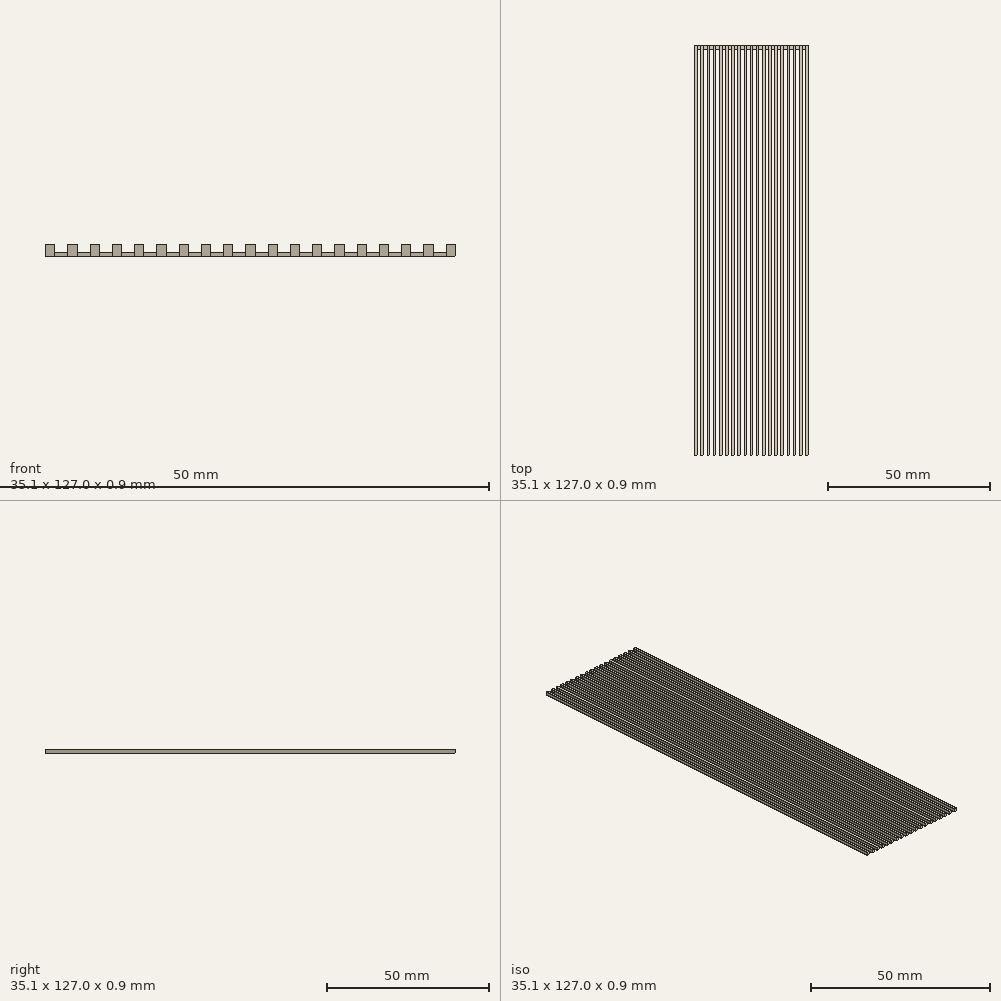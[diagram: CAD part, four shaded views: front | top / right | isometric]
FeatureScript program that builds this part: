
annotation { "Feature Type Name" : "Feature", "Feature Type Description" : "" }
export const myFeature = defineFeature(function(context is Context, id is Id, definition is map)
    precondition{}
    {
        {
            var Q0;
            Q0=qCreatedBy(makeId("Front.planeOp"),FACE);
            var sketch = newSketch(context, id + "F0", { "sketchPlane" : qUnion([Q0])});
            skLineSegment(sketch, "E0.bottom", {"start": v(0.4, -0.47) * mm, "end": v(-0.4, -0.47) * mm});
            skLineSegment(sketch, "E0.top", {"start": v(0.4, 0.47) * mm, "end": v(-0.4, 0.47) * mm});
            skLineSegment(sketch, "E0.left", {"start": v(0.4, -0.47) * mm, "end": v(0.4, 0.47) * mm});
            skLineSegment(sketch, "E0.right", {"start": v(-0.4, -0.47) * mm, "end": v(-0.4, 0.47) * mm});
            skPoint(sketch, "E0.middle", {"position": v(0, 0) * mm});
            skLineSegment(sketch, "E1.1.0.0", {"start": v(2.3, -0.47) * mm, "end": v(2.3, 0.47) * mm});
            skLineSegment(sketch, "E1.1.0.1", {"start": v(2.3, 0.47) * mm, "end": v(1.5, 0.47) * mm});
            skLineSegment(sketch, "E1.1.0.2", {"start": v(1.5, -0.47) * mm, "end": v(1.5, 0.47) * mm});
            skLineSegment(sketch, "E1.1.0.3", {"start": v(2.3, -0.47) * mm, "end": v(1.5, -0.47) * mm});
            skLineSegment(sketch, "E1.2.0.0", {"start": v(4.21, -0.47) * mm, "end": v(4.21, 0.47) * mm});
            skLineSegment(sketch, "E1.2.0.1", {"start": v(4.21, 0.47) * mm, "end": v(3.4, 0.47) * mm});
            skLineSegment(sketch, "E1.2.0.2", {"start": v(3.4, -0.47) * mm, "end": v(3.4, 0.47) * mm});
            skLineSegment(sketch, "E1.2.0.3", {"start": v(4.21, -0.47) * mm, "end": v(3.4, -0.47) * mm});
            skLineSegment(sketch, "E1.3.0.0", {"start": v(6.12, -0.47) * mm, "end": v(6.12, 0.47) * mm});
            skLineSegment(sketch, "E1.3.0.1", {"start": v(6.12, 0.47) * mm, "end": v(5.31, 0.47) * mm});
            skLineSegment(sketch, "E1.3.0.2", {"start": v(5.31, -0.47) * mm, "end": v(5.31, 0.47) * mm});
            skLineSegment(sketch, "E1.3.0.3", {"start": v(6.12, -0.47) * mm, "end": v(5.31, -0.47) * mm});
            skLineSegment(sketch, "E1.4.0.0", {"start": v(8.02, -0.47) * mm, "end": v(8.02, 0.47) * mm});
            skLineSegment(sketch, "E1.4.0.1", {"start": v(8.02, 0.47) * mm, "end": v(7.22, 0.47) * mm});
            skLineSegment(sketch, "E1.4.0.2", {"start": v(7.22, -0.47) * mm, "end": v(7.22, 0.47) * mm});
            skLineSegment(sketch, "E1.4.0.3", {"start": v(8.02, -0.47) * mm, "end": v(7.22, -0.47) * mm});
            skLineSegment(sketch, "E1.5.0.0", {"start": v(9.93, -0.47) * mm, "end": v(9.93, 0.47) * mm});
            skLineSegment(sketch, "E1.5.0.1", {"start": v(9.93, 0.47) * mm, "end": v(9.12, 0.47) * mm});
            skLineSegment(sketch, "E1.5.0.2", {"start": v(9.12, -0.47) * mm, "end": v(9.12, 0.47) * mm});
            skLineSegment(sketch, "E1.5.0.3", {"start": v(9.93, -0.47) * mm, "end": v(9.12, -0.47) * mm});
            skLineSegment(sketch, "E1.6.0.0", {"start": v(11.83, -0.47) * mm, "end": v(11.83, 0.47) * mm});
            skLineSegment(sketch, "E1.6.0.1", {"start": v(11.83, 0.47) * mm, "end": v(11.03, 0.47) * mm});
            skLineSegment(sketch, "E1.6.0.2", {"start": v(11.03, -0.47) * mm, "end": v(11.03, 0.47) * mm});
            skLineSegment(sketch, "E1.6.0.3", {"start": v(11.83, -0.47) * mm, "end": v(11.03, -0.47) * mm});
            skLineSegment(sketch, "E1.7.0.0", {"start": v(13.74, -0.47) * mm, "end": v(13.74, 0.47) * mm});
            skLineSegment(sketch, "E1.7.0.1", {"start": v(13.74, 0.47) * mm, "end": v(12.93, 0.47) * mm});
            skLineSegment(sketch, "E1.7.0.2", {"start": v(12.93, -0.47) * mm, "end": v(12.93, 0.47) * mm});
            skLineSegment(sketch, "E1.7.0.3", {"start": v(13.74, -0.47) * mm, "end": v(12.93, -0.47) * mm});
            skLineSegment(sketch, "E1.8.0.0", {"start": v(15.64, -0.47) * mm, "end": v(15.64, 0.47) * mm});
            skLineSegment(sketch, "E1.8.0.1", {"start": v(15.64, 0.47) * mm, "end": v(14.84, 0.47) * mm});
            skLineSegment(sketch, "E1.8.0.2", {"start": v(14.84, -0.47) * mm, "end": v(14.84, 0.47) * mm});
            skLineSegment(sketch, "E1.8.0.3", {"start": v(15.64, -0.47) * mm, "end": v(14.84, -0.47) * mm});
            skLineSegment(sketch, "E1.9.0.0", {"start": v(17.55, -0.47) * mm, "end": v(17.55, 0.47) * mm});
            skLineSegment(sketch, "E1.9.0.1", {"start": v(17.55, 0.47) * mm, "end": v(16.74, 0.47) * mm});
            skLineSegment(sketch, "E1.9.0.2", {"start": v(16.74, -0.47) * mm, "end": v(16.74, 0.47) * mm});
            skLineSegment(sketch, "E1.9.0.3", {"start": v(17.55, -0.47) * mm, "end": v(16.74, -0.47) * mm});
            skLineSegment(sketch, "E1.10.0.0", {"start": v(19.45, -0.47) * mm, "end": v(19.45, 0.47) * mm});
            skLineSegment(sketch, "E1.10.0.1", {"start": v(19.45, 0.47) * mm, "end": v(18.65, 0.47) * mm});
            skLineSegment(sketch, "E1.10.0.2", {"start": v(18.65, -0.47) * mm, "end": v(18.65, 0.47) * mm});
            skLineSegment(sketch, "E1.10.0.3", {"start": v(19.45, -0.47) * mm, "end": v(18.65, -0.47) * mm});
            skLineSegment(sketch, "E1.11.0.0", {"start": v(21.36, -0.47) * mm, "end": v(21.36, 0.47) * mm});
            skLineSegment(sketch, "E1.11.0.1", {"start": v(21.36, 0.47) * mm, "end": v(20.55, 0.47) * mm});
            skLineSegment(sketch, "E1.11.0.2", {"start": v(20.55, -0.47) * mm, "end": v(20.55, 0.47) * mm});
            skLineSegment(sketch, "E1.11.0.3", {"start": v(21.36, -0.47) * mm, "end": v(20.55, -0.47) * mm});
            skLineSegment(sketch, "E1.12.0.0", {"start": v(23.26, -0.47) * mm, "end": v(23.26, 0.47) * mm});
            skLineSegment(sketch, "E1.12.0.1", {"start": v(23.26, 0.47) * mm, "end": v(22.46, 0.47) * mm});
            skLineSegment(sketch, "E1.12.0.2", {"start": v(22.46, -0.47) * mm, "end": v(22.46, 0.47) * mm});
            skLineSegment(sketch, "E1.12.0.3", {"start": v(23.26, -0.47) * mm, "end": v(22.46, -0.47) * mm});
            skLineSegment(sketch, "E1.13.0.0", {"start": v(25.17, -0.47) * mm, "end": v(25.17, 0.47) * mm});
            skLineSegment(sketch, "E1.13.0.1", {"start": v(25.17, 0.47) * mm, "end": v(24.36, 0.47) * mm});
            skLineSegment(sketch, "E1.13.0.2", {"start": v(24.36, -0.47) * mm, "end": v(24.36, 0.47) * mm});
            skLineSegment(sketch, "E1.13.0.3", {"start": v(25.17, -0.47) * mm, "end": v(24.36, -0.47) * mm});
            skLineSegment(sketch, "E1.14.0.0", {"start": v(27.07, -0.47) * mm, "end": v(27.07, 0.47) * mm});
            skLineSegment(sketch, "E1.14.0.1", {"start": v(27.07, 0.47) * mm, "end": v(26.27, 0.47) * mm});
            skLineSegment(sketch, "E1.14.0.2", {"start": v(26.27, -0.47) * mm, "end": v(26.27, 0.47) * mm});
            skLineSegment(sketch, "E1.14.0.3", {"start": v(27.07, -0.47) * mm, "end": v(26.27, -0.47) * mm});
            skLineSegment(sketch, "E1.15.0.0", {"start": v(28.98, -0.47) * mm, "end": v(28.98, 0.47) * mm});
            skLineSegment(sketch, "E1.15.0.1", {"start": v(28.98, 0.47) * mm, "end": v(28.17, 0.47) * mm});
            skLineSegment(sketch, "E1.15.0.2", {"start": v(28.17, -0.47) * mm, "end": v(28.17, 0.47) * mm});
            skLineSegment(sketch, "E1.15.0.3", {"start": v(28.98, -0.47) * mm, "end": v(28.17, -0.47) * mm});
            skLineSegment(sketch, "E1.16.0.0", {"start": v(30.88, -0.47) * mm, "end": v(30.88, 0.47) * mm});
            skLineSegment(sketch, "E1.16.0.1", {"start": v(30.88, 0.47) * mm, "end": v(30.08, 0.47) * mm});
            skLineSegment(sketch, "E1.16.0.2", {"start": v(30.08, -0.47) * mm, "end": v(30.08, 0.47) * mm});
            skLineSegment(sketch, "E1.16.0.3", {"start": v(30.88, -0.47) * mm, "end": v(30.08, -0.47) * mm});
            skLineSegment(sketch, "E1.17.0.0", {"start": v(32.79, -0.47) * mm, "end": v(32.79, 0.47) * mm});
            skLineSegment(sketch, "E1.17.0.1", {"start": v(32.79, 0.47) * mm, "end": v(31.98, 0.47) * mm});
            skLineSegment(sketch, "E1.17.0.2", {"start": v(31.98, -0.47) * mm, "end": v(31.98, 0.47) * mm});
            skLineSegment(sketch, "E1.17.0.3", {"start": v(32.79, -0.47) * mm, "end": v(31.98, -0.47) * mm});
            skLineSegment(sketch, "E1.18.0.0", {"start": v(34.7, -0.47) * mm, "end": v(34.7, 0.47) * mm});
            skLineSegment(sketch, "E1.18.0.1", {"start": v(34.7, 0.47) * mm, "end": v(33.89, 0.47) * mm});
            skLineSegment(sketch, "E1.18.0.2", {"start": v(33.89, -0.47) * mm, "end": v(33.89, 0.47) * mm});
            skLineSegment(sketch, "E1.18.0.3", {"start": v(34.7, -0.47) * mm, "end": v(33.89, -0.47) * mm});
            skLineSegment(sketch, "E1.direction1", {"start": v(0.4, -0.47) * mm, "end": v(2.3, -0.47) * mm, "construction": true});
            skSolve(sketch);
        }
        {
            var Q0;
            Q0=makeQuery(id+"F0.imprint","IMPRINT",FACE,{"disambiguationData":[TD([[makeQuery(id+"F0.imprint","IMPRINT",EDGE,{"derivedFrom":sQuery(id+"F0.wireOp",EDGE,"E0.bottom")}),-1.0]])]});
            var Q1;
            Q1=makeQuery(id+"F0.imprint","IMPRINT",FACE,{"disambiguationData":[TD([[makeQuery(id+"F0.imprint","IMPRINT",EDGE,{"derivedFrom":sQuery(id+"F0.wireOp",EDGE,"E1.1.0.0")}),1.0]])]});
            var Q2;
            Q2=makeQuery(id+"F0.imprint","IMPRINT",FACE,{"disambiguationData":[TD([[makeQuery(id+"F0.imprint","IMPRINT",EDGE,{"derivedFrom":sQuery(id+"F0.wireOp",EDGE,"E1.2.0.0")}),1.0]])]});
            var Q3;
            Q3=makeQuery(id+"F0.imprint","IMPRINT",FACE,{"disambiguationData":[TD([[makeQuery(id+"F0.imprint","IMPRINT",EDGE,{"derivedFrom":sQuery(id+"F0.wireOp",EDGE,"E1.3.0.0")}),1.0]])]});
            var Q4;
            Q4=makeQuery(id+"F0.imprint","IMPRINT",FACE,{"disambiguationData":[TD([[makeQuery(id+"F0.imprint","IMPRINT",EDGE,{"derivedFrom":sQuery(id+"F0.wireOp",EDGE,"E1.4.0.0")}),1.0]])]});
            var Q5;
            Q5=makeQuery(id+"F0.imprint","IMPRINT",FACE,{"disambiguationData":[TD([[makeQuery(id+"F0.imprint","IMPRINT",EDGE,{"derivedFrom":sQuery(id+"F0.wireOp",EDGE,"E1.5.0.0")}),1.0]])]});
            var Q6;
            Q6=makeQuery(id+"F0.imprint","IMPRINT",FACE,{"disambiguationData":[TD([[makeQuery(id+"F0.imprint","IMPRINT",EDGE,{"derivedFrom":sQuery(id+"F0.wireOp",EDGE,"E1.6.0.0")}),1.0]])]});
            var Q7;
            Q7=makeQuery(id+"F0.imprint","IMPRINT",FACE,{"disambiguationData":[TD([[makeQuery(id+"F0.imprint","IMPRINT",EDGE,{"derivedFrom":sQuery(id+"F0.wireOp",EDGE,"E1.7.0.0")}),1.0]])]});
            var Q8;
            Q8=makeQuery(id+"F0.imprint","IMPRINT",FACE,{"disambiguationData":[TD([[makeQuery(id+"F0.imprint","IMPRINT",EDGE,{"derivedFrom":sQuery(id+"F0.wireOp",EDGE,"E1.8.0.0")}),1.0]])]});
            var Q9;
            Q9=makeQuery(id+"F0.imprint","IMPRINT",FACE,{"disambiguationData":[TD([[makeQuery(id+"F0.imprint","IMPRINT",EDGE,{"derivedFrom":sQuery(id+"F0.wireOp",EDGE,"E1.9.0.0")}),1.0]])]});
            var Q10;
            Q10=makeQuery(id+"F0.imprint","IMPRINT",FACE,{"disambiguationData":[TD([[makeQuery(id+"F0.imprint","IMPRINT",EDGE,{"derivedFrom":sQuery(id+"F0.wireOp",EDGE,"E1.10.0.0")}),1.0]])]});
            var Q11;
            Q11=makeQuery(id+"F0.imprint","IMPRINT",FACE,{"disambiguationData":[TD([[makeQuery(id+"F0.imprint","IMPRINT",EDGE,{"derivedFrom":sQuery(id+"F0.wireOp",EDGE,"E1.11.0.0")}),1.0]])]});
            var Q12;
            Q12=makeQuery(id+"F0.imprint","IMPRINT",FACE,{"disambiguationData":[TD([[makeQuery(id+"F0.imprint","IMPRINT",EDGE,{"derivedFrom":sQuery(id+"F0.wireOp",EDGE,"E1.12.0.0")}),1.0]])]});
            var Q13;
            Q13=makeQuery(id+"F0.imprint","IMPRINT",FACE,{"disambiguationData":[TD([[makeQuery(id+"F0.imprint","IMPRINT",EDGE,{"derivedFrom":sQuery(id+"F0.wireOp",EDGE,"E1.13.0.0")}),1.0]])]});
            var Q14;
            Q14=makeQuery(id+"F0.imprint","IMPRINT",FACE,{"disambiguationData":[TD([[makeQuery(id+"F0.imprint","IMPRINT",EDGE,{"derivedFrom":sQuery(id+"F0.wireOp",EDGE,"E1.14.0.0")}),1.0]])]});
            var Q15;
            Q15=makeQuery(id+"F0.imprint","IMPRINT",FACE,{"disambiguationData":[TD([[makeQuery(id+"F0.imprint","IMPRINT",EDGE,{"derivedFrom":sQuery(id+"F0.wireOp",EDGE,"E1.15.0.0")}),1.0]])]});
            var Q16;
            Q16=makeQuery(id+"F0.imprint","IMPRINT",FACE,{"disambiguationData":[TD([[makeQuery(id+"F0.imprint","IMPRINT",EDGE,{"derivedFrom":sQuery(id+"F0.wireOp",EDGE,"E1.16.0.0")}),1.0]])]});
            var Q17;
            Q17=makeQuery(id+"F0.imprint","IMPRINT",FACE,{"disambiguationData":[TD([[makeQuery(id+"F0.imprint","IMPRINT",EDGE,{"derivedFrom":sQuery(id+"F0.wireOp",EDGE,"E1.17.0.0")}),1.0]])]});
            var Q18;
            Q18=makeQuery(id+"F0.imprint","IMPRINT",FACE,{"disambiguationData":[TD([[makeQuery(id+"F0.imprint","IMPRINT",EDGE,{"derivedFrom":sQuery(id+"F0.wireOp",EDGE,"E1.18.0.0")}),1.0]])]});
            extrude(context, id + "F1", {"entities" : qUnion([Q0, Q1, Q2, Q3, Q4, Q5, Q6, Q7, Q8, Q9, Q10, Q11, Q12, Q13, Q14, Q15, Q16, Q17, Q18]), "depth" : 127 * mm, "offsetDistance" : 25.4 * mm});
        }
        {
            var Q0;
            Q0=qCreatedBy(makeId("Front.planeOp"),FACE);
            var sketch = newSketch(context, id + "F2", { "sketchPlane" : qUnion([Q0])});
            skLineSegment(sketch, "E2.0", {"start": v(0.4, -0.47) * mm, "end": v(-0.4, -0.47) * mm});
            skLineSegment(sketch, "E3.bottom", {"start": v(-0.4, -0.47) * mm, "end": v(34.65, -0.47) * mm});
            skLineSegment(sketch, "E3.top", {"start": v(-0.4, -0.19) * mm, "end": v(34.65, -0.19) * mm});
            skLineSegment(sketch, "E3.left", {"start": v(-0.4, -0.47) * mm, "end": v(-0.4, -0.19) * mm});
            skLineSegment(sketch, "E3.right", {"start": v(34.65, -0.47) * mm, "end": v(34.65, -0.19) * mm});
            skSolve(sketch);
        }
        {
            var Q0;
            Q0 = qSketchRegion(id + "F2", true);
            extrude(context, id + "F3", {"entities" : qUnion([Q0]), "operationType" : NewBodyOperationType.ADD, "depth" : 1.27 * mm, "offsetDistance" : 25.4 * mm});
        }
    });
